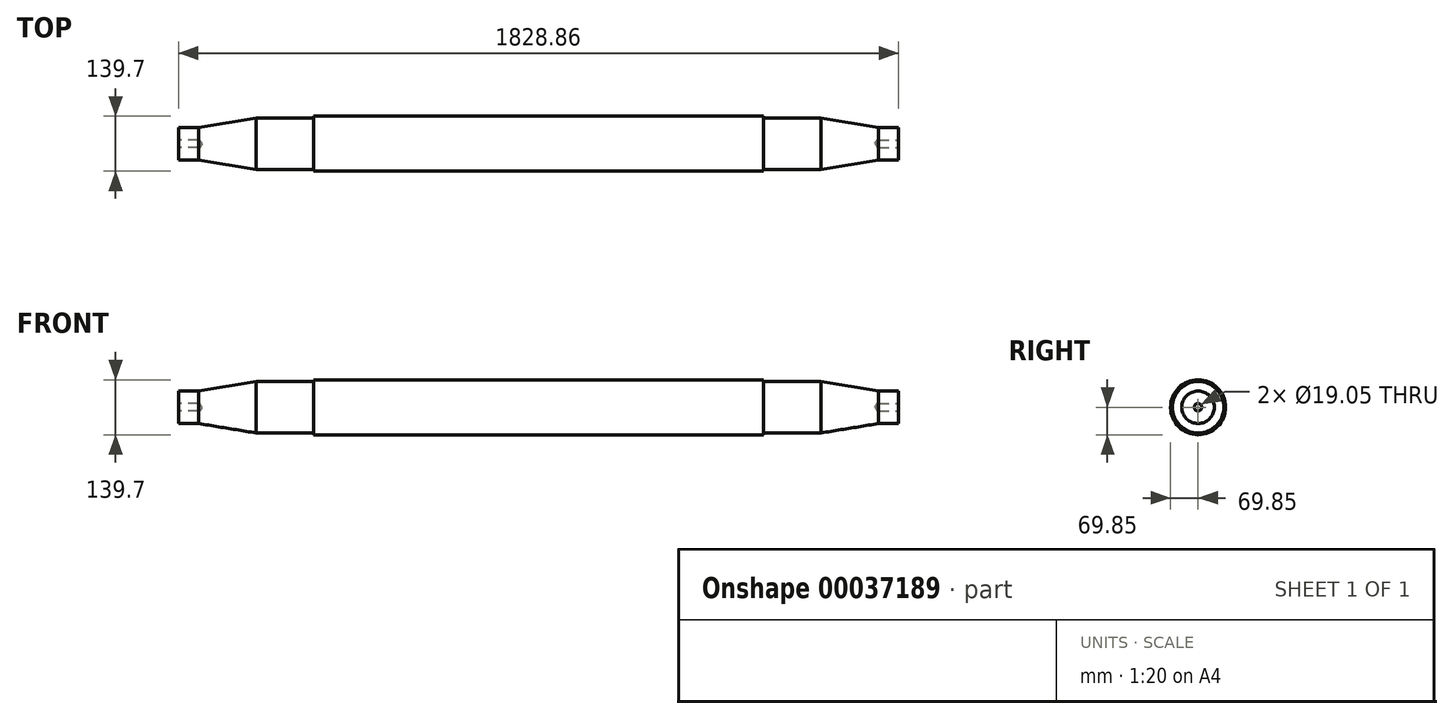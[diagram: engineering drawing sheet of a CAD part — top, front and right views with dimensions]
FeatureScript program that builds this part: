
annotation { "Feature Type Name" : "Feature", "Feature Type Description" : "" }
export const myFeature = defineFeature(function(context is Context, id is Id, definition is map)
    precondition{}
    {
        {
            var Q0;
            Q0=qCreatedBy(makeId("Right.planeOp"),FACE);
            var sketch = newSketch(context, id + "F0", { "sketchPlane" : qUnion([Q0])});
            skCircle(sketch, "E0", {"center": v(0, 0) * mm, "radius": 69.85 * mm});
            skSolve(sketch);
        }
        {
            var Q0;
            Q0=qSketchRegion(id+"F0",true);
            extrude(context, id + "F1", {"entities" : qUnion([Q0]), "endBound" : BoundingType.SYMMETRIC, "depth" : 1143 * mm});
        }
        {
            var Q0;
            Q0=makeQuery(id+"F1.opExtrude","CAP_FACE",FACE,{"disambiguationData":[OSD([sQuery(id+"F0.wireOp",EDGE,"E0")])],"isStart":false});
            var sketch = newSketch(context, id + "F2", { "sketchPlane" : qUnion([Q0])});
            skCircle(sketch, "E1", {"center": v(0, 0) * mm, "radius": 65.4 * mm});
            skSolve(sketch);
        }
        {
            var Q0;
            Q0=qSketchRegion(id+"F2",true);
            extrude(context, id + "F3", {"entities" : qUnion([Q0]), "depth" : 146.08 * mm});
        }
        {
            var Q0;
            Q0=makeQuery(id+"F3.opExtrude","CAP_FACE",FACE,{"disambiguationData":[OSD([sQuery(id+"F2.wireOp",EDGE,"E1")])],"isStart":false});
            cPlane(context, id + "F4", {"entities" : qUnion([Q0]), "cplaneType" : CPlaneType.OFFSET, "offset" : 146.05 * mm, "width" : 152.4 * mm, "height" : 152.4 * mm});
        }
        {
            var Q0;
            Q0=qCreatedBy(id+"F4.planeOp",FACE);
            var sketch = newSketch(context, id + "F5", { "sketchPlane" : qUnion([Q0])});
            skCircle(sketch, "E2", {"center": v(0, 0) * mm, "radius": 41.28 * mm});
            skSolve(sketch);
        }
        {
            var Q1;
            Q1=makeQuery(id+"F3.opExtrude","CAP_FACE",FACE,{"disambiguationData":[OSD([sQuery(id+"F2.wireOp",EDGE,"E1")])],"isStart":false});
            var Q2;
            Q2=makeQuery(id+"F5.imprint","IMPRINT",FACE,{"disambiguationData":[TD([[makeQuery(id+"F5.imprint","IMPRINT",EDGE,{"derivedFrom":sQuery(id+"F5.wireOp",EDGE,"E2")}),1.0]])]});
            loft(context, id + "F6", {"operationType" : NewBodyOperationType.ADD, "sheetProfilesArray" : [{ "sheetProfileEntities" : qUnion([Q1]) }, { "sheetProfileEntities" : qUnion([Q2]) }]});
        }
        {
            var Q0;
            Q0=makeQuery(id+"F6.opLoft","CAP_FACE",FACE,{"disambiguationData":[OSD([makeQuery(id+"F5.imprint","IMPRINT",FACE,{"disambiguationData":[TD([[makeQuery(id+"F5.imprint","IMPRINT",EDGE,{"derivedFrom":sQuery(id+"F5.wireOp",EDGE,"E2")}),1.0]])]})])],"isStart":true});
            var sketch = newSketch(context, id + "F7", { "sketchPlane" : qUnion([Q0])});
            skCircle(sketch, "E3.0", {"center": v(0, 0) * mm, "radius": 41.28 * mm});
            skSolve(sketch);
        }
        {
            var Q0;
            Q0=qSketchRegion(id+"F7",true);
            extrude(context, id + "F8", {"entities" : qUnion([Q0]), "operationType" : NewBodyOperationType.ADD, "depth" : 50.8 * mm});
        }
        {
            var Q0;
            Q0=makeQuery(id+"F8.opExtrude","CAP_FACE",FACE,{"disambiguationData":[OSD([sQuery(id+"F7.wireOp",EDGE,"E3.0")])],"isStart":false});
            var sketch = newSketch(context, id + "F9", { "sketchPlane" : qUnion([Q0])});
            skPoint(sketch, "E4", {"position": v(0, 0) * mm});
            skSolve(sketch);
        }
        {
            var Q0;
            Q0=sQuery(id+"F9.wireOp",VERTEX,"E4");
            var Q1;
            Q1=makeQuery(id+"F3.opExtrude","SWEPT_BODY",BODY,{"disambiguationData":[OSD([sQuery(id+"F2.wireOp",EDGE,"E1")])]});
            hole(context, id + "F10", {"style" : HoleStyle.SIMPLE, "holeDiameter" : 19.05 * mm, "endStyle" : HoleEndStyle.BLIND, "holeDepth" : 53.97 * mm, "locations" : qUnion([Q0]), "scope" : qUnion([Q1])});
        }
        {
            var Q0;
            Q0=makeQuery(id+"F3.opExtrude","SWEPT_BODY",BODY,{"disambiguationData":[OSD([sQuery(id+"F2.wireOp",EDGE,"E1")])]});
            var Q1;
            Q1=qCreatedBy(makeId("Right.planeOp"),FACE);
            mirror(context, id + "F11", {"operationType" : NewBodyOperationType.ADD, "entities" : qUnion([Q0]), "mirrorPlane" : qUnion([Q1])});
        }
    });
